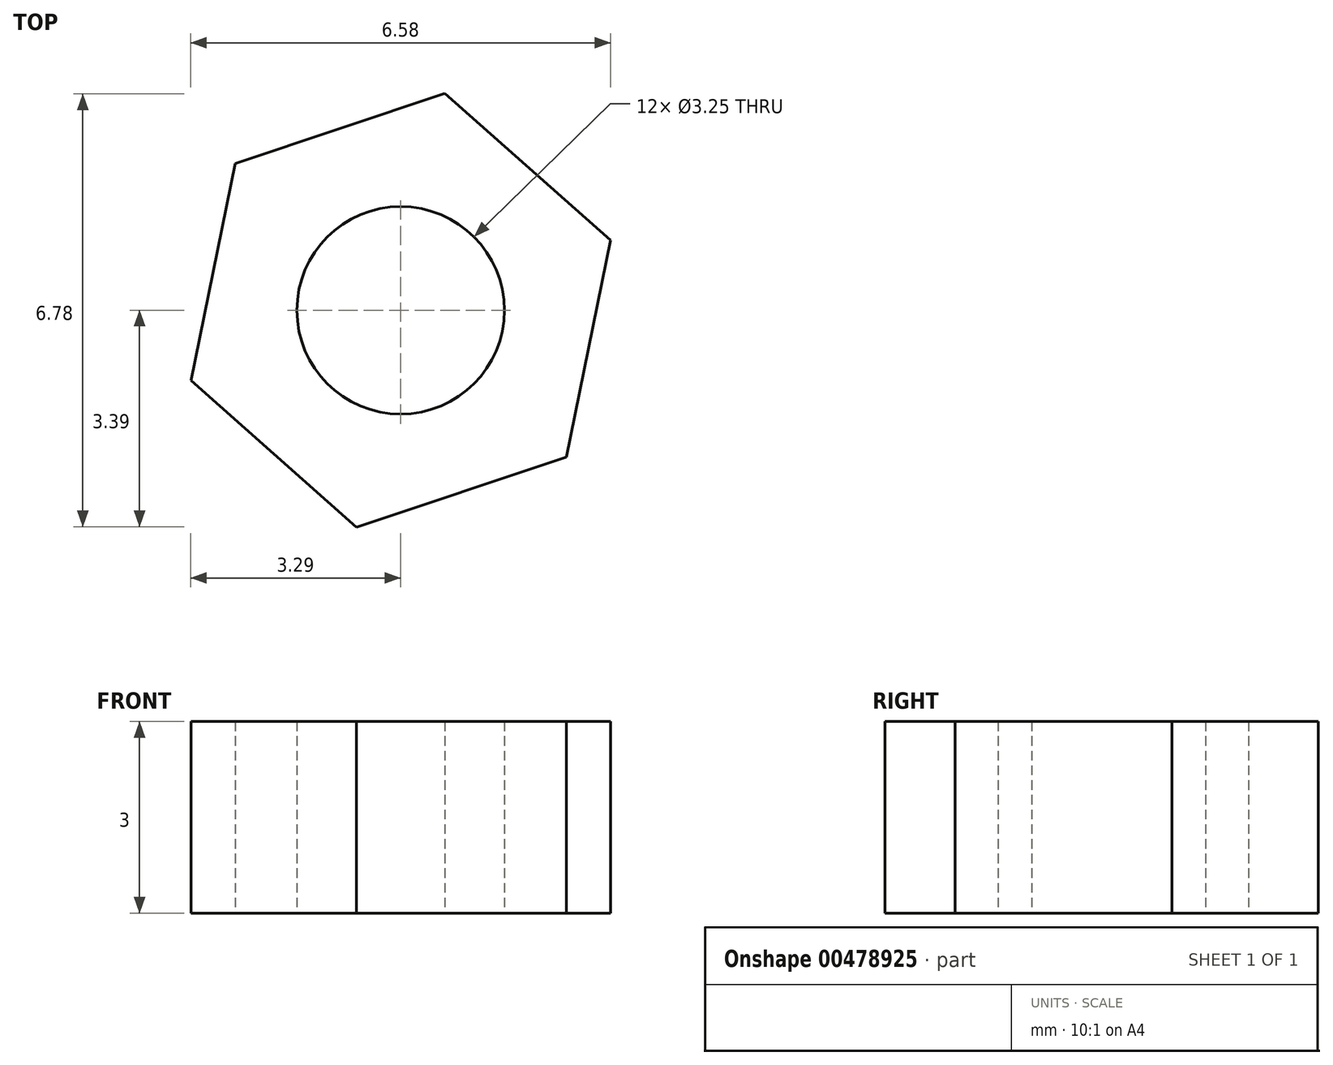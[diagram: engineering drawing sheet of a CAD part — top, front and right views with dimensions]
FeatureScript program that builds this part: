
annotation { "Feature Type Name" : "Feature", "Feature Type Description" : "" }
export const myFeature = defineFeature(function(context is Context, id is Id, definition is map)
    precondition{}
    {
        {
            var Q0;
            Q0=qCreatedBy(makeId("Top.planeOp"),FACE);
            var sketch = newSketch(context, id + "F0", { "sketchPlane" : qUnion([Q0])});
            skCircle(sketch, "E0", {"center": v(0, 0) * mm, "radius": 1.63 * mm});
            skCircle(sketch, "E1.cCircle", {"center": v(0, 0) * mm, "radius": 3 * mm, "construction": true});
            skLineSegment(sketch, "E1.0", {"start": v(3.29, 1.1) * mm, "end": v(2.6, -2.3) * mm});
            skLineSegment(sketch, "E1.1", {"start": v(2.6, -2.3) * mm, "end": v(-0.7, -3.4) * mm});
            skLineSegment(sketch, "E1.2", {"start": v(-0.7, -3.4) * mm, "end": v(-3.29, -1.1) * mm});
            skLineSegment(sketch, "E1.3", {"start": v(-3.29, -1.1) * mm, "end": v(-2.6, 2.3) * mm});
            skLineSegment(sketch, "E1.4", {"start": v(-2.6, 2.3) * mm, "end": v(0.7, 3.4) * mm});
            skLineSegment(sketch, "E1.5", {"start": v(0.7, 3.4) * mm, "end": v(3.29, 1.1) * mm});
            skPoint(sketch, "E1.0.midPoint", {"position": v(2.94, -0.6) * mm});
            skSolve(sketch);
        }
        {
            var Q0;
            Q0 = qSketchRegion(id + "F0", true);
            extrude(context, id + "F1", {"entities" : qUnion([Q0]), "depth" : 3 * mm, "offsetDistance" : 25 * mm});
        }
    });
